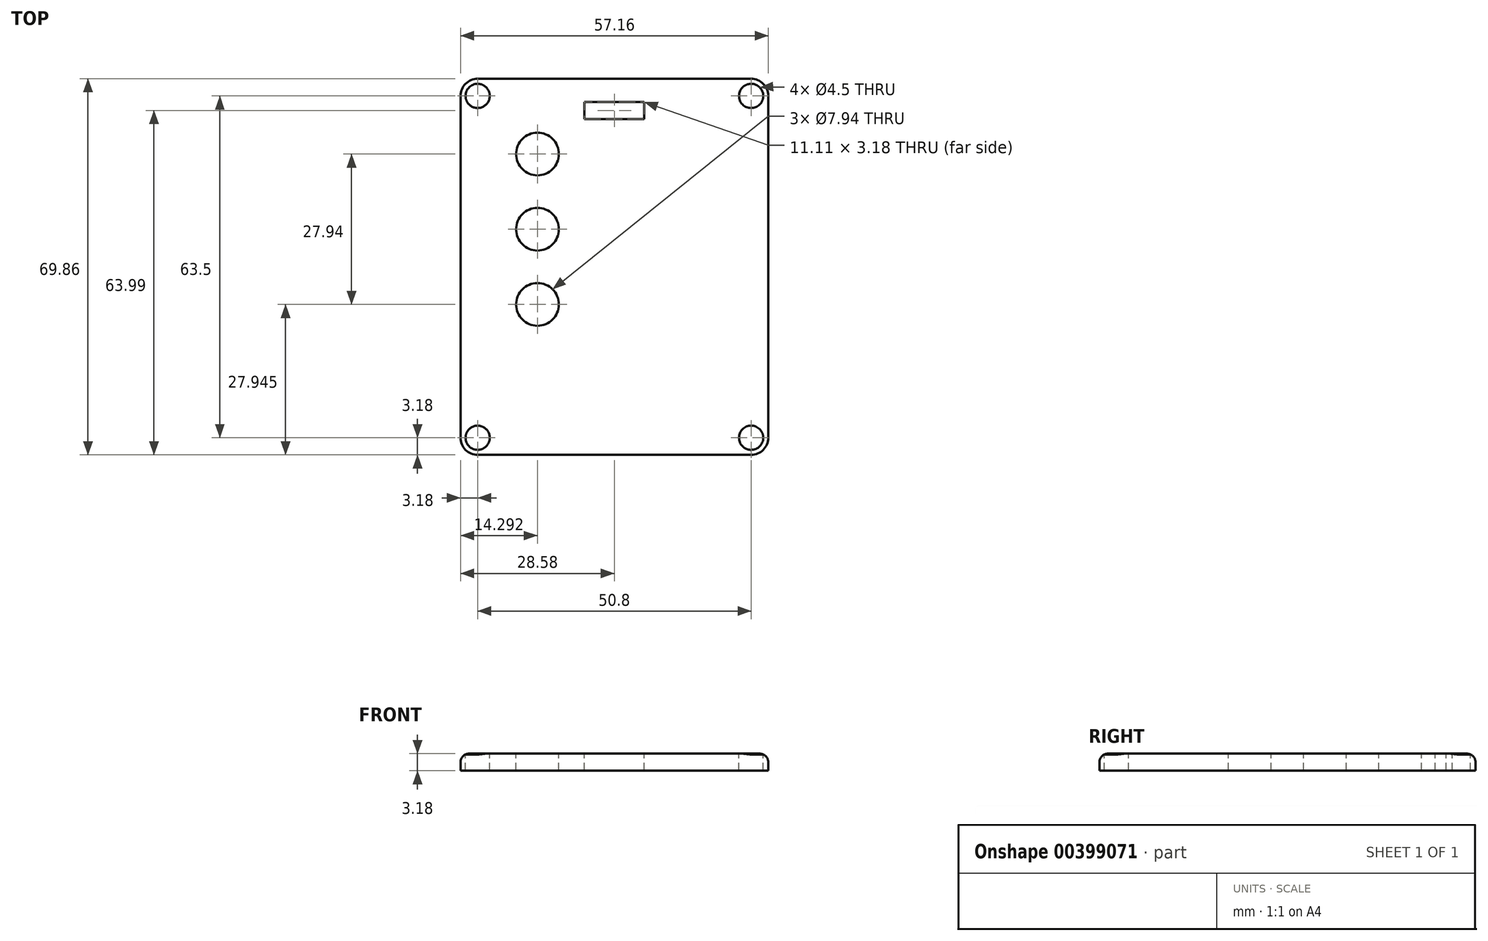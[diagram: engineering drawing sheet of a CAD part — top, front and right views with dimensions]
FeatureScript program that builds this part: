
annotation { "Feature Type Name" : "Feature", "Feature Type Description" : "" }
export const myFeature = defineFeature(function(context is Context, id is Id, definition is map)
    precondition{}
    {
        {
            var Q0;
            Q0=qCreatedBy(makeId("Top.planeOp"),FACE);
            var sketch = newSketch(context, id + "F0", { "sketchPlane" : qUnion([Q0])});
            skLineSegment(sketch, "E0.bottom", {"start": v(-25.4, 34.93) * mm, "end": v(25.4, 34.93) * mm});
            skLineSegment(sketch, "E0.top", {"start": v(-25.4, -34.93) * mm, "end": v(25.4, -34.93) * mm});
            skLineSegment(sketch, "E0.left", {"start": v(-28.58, 31.75) * mm, "end": v(-28.58, -31.75) * mm});
            skLineSegment(sketch, "E0.right", {"start": v(28.57, 31.75) * mm, "end": v(28.58, -31.75) * mm});
            skPoint(sketch, "E1.visualSharp", {"position": v(-28.58, 34.93) * mm});
            skArc(sketch, "E1.filletArc", {"start": v(-25.4, 34.93) * mm, "mid": v(-27.65, 34) * mm, "end": v(-28.58, 31.75) * mm});
            skPoint(sketch, "E2.visualSharp", {"position": v(28.57, 34.93) * mm});
            skArc(sketch, "E2.filletArc", {"start": v(28.57, 31.75) * mm, "mid": v(27.65, 34) * mm, "end": v(25.4, 34.92) * mm});
            skPoint(sketch, "E3.visualSharp", {"position": v(28.58, -34.93) * mm});
            skArc(sketch, "E3.filletArc", {"start": v(25.4, -34.93) * mm, "mid": v(27.65, -34) * mm, "end": v(28.58, -31.75) * mm});
            skPoint(sketch, "E4.visualSharp", {"position": v(-28.58, -34.93) * mm});
            skArc(sketch, "E4.filletArc", {"start": v(-28.58, -31.75) * mm, "mid": v(-27.65, -34) * mm, "end": v(-25.4, -34.93) * mm});
            skSolve(sketch);
        }
        {
            var Q0;
            Q0 = qSketchRegion(id + "F0", true);
            extrude(context, id + "F1", {"entities" : qUnion([Q0]), "depth" : 3.17 * mm});
        }
        {
            var Q0;
            Q0=makeQuery(id+"F1.opExtrude","CAP_EDGE",EDGE,{"disambiguationData":[OSD([sQuery(id+"F0.wireOp",EDGE,"E0.top")])],"isStart":false});
            var Q1;
            Q1=makeQuery(id+"F1.opExtrude","CAP_EDGE",EDGE,{"disambiguationData":[OSD([sQuery(id+"F0.wireOp",EDGE,"E0.left")])],"isStart":false});
            fillet(context, id + "F2", {"entities" : qUnion([Q0, Q1]), "radius" : 1.59 * mm, "tangentPropagation" : true, "allowEdgeOverflow" : false});
        }
        {
            var Q0;
            Q0=makeQuery(id+"F1.opExtrude","CAP_FACE",FACE,{"disambiguationData":[OSD([sQuery(id+"F0.wireOp",EDGE,"E0.bottom"),sQuery(id+"F0.wireOp",EDGE,"E0.top"),sQuery(id+"F0.wireOp",EDGE,"E0.left"),sQuery(id+"F0.wireOp",EDGE,"E0.right"),sQuery(id+"F0.wireOp",EDGE,"E1.filletArc"),sQuery(id+"F0.wireOp",EDGE,"E2.filletArc"),sQuery(id+"F0.wireOp",EDGE,"E3.filletArc"),sQuery(id+"F0.wireOp",EDGE,"E4.filletArc")])],"isStart":false});
            var sketch = newSketch(context, id + "F3", { "sketchPlane" : qUnion([Q0])});
            skCircle(sketch, "E5", {"center": v(-25.4, 31.75) * mm, "radius": 2.25 * mm});
            skCircle(sketch, "E6", {"center": v(25.4, 31.75) * mm, "radius": 2.25 * mm});
            skCircle(sketch, "E7", {"center": v(25.4, -31.75) * mm, "radius": 2.25 * mm});
            skCircle(sketch, "E8", {"center": v(-25.4, -31.75) * mm, "radius": 2.25 * mm});
            skSolve(sketch);
        }
        {
            var Q0;
            Q0 = qSketchRegion(id + "F3", true);
            extrude(context, id + "F4", {"entities" : qUnion([Q0]), "operationType" : NewBodyOperationType.REMOVE, "endBound" : BoundingType.THROUGH_ALL, "oppositeDirection" : true, "depth" : 25.4 * mm});
        }
        {
            var Q0;
            Q0=makeQuery(id+"F1.opExtrude","CAP_FACE",FACE,{"disambiguationData":[OSD([sQuery(id+"F0.wireOp",EDGE,"E0.bottom"),sQuery(id+"F0.wireOp",EDGE,"E0.top"),sQuery(id+"F0.wireOp",EDGE,"E0.left"),sQuery(id+"F0.wireOp",EDGE,"E0.right"),sQuery(id+"F0.wireOp",EDGE,"E1.filletArc"),sQuery(id+"F0.wireOp",EDGE,"E2.filletArc"),sQuery(id+"F0.wireOp",EDGE,"E3.filletArc"),sQuery(id+"F0.wireOp",EDGE,"E4.filletArc")])],"isStart":false});
            var sketch = newSketch(context, id + "F5", { "sketchPlane" : qUnion([Q0])});
            skCircle(sketch, "E9", {"center": v(-14.29, -6.98) * mm, "radius": 3.97 * mm});
            skCircle(sketch, "E10", {"center": v(-14.29, 6.98) * mm, "radius": 3.97 * mm});
            skCircle(sketch, "E11", {"center": v(-14.29, 20.96) * mm, "radius": 3.97 * mm});
            skLineSegment(sketch, "E12.bottom", {"start": v(-5.56, 30.65) * mm, "end": v(5.56, 30.65) * mm});
            skLineSegment(sketch, "E12.top", {"start": v(-5.56, 27.47) * mm, "end": v(5.56, 27.47) * mm});
            skLineSegment(sketch, "E12.left", {"start": v(-5.56, 30.65) * mm, "end": v(-5.56, 27.47) * mm});
            skLineSegment(sketch, "E12.right", {"start": v(5.56, 30.65) * mm, "end": v(5.56, 27.47) * mm});
            skSolve(sketch);
        }
        {
            var Q0;
            Q0 = qSketchRegion(id + "F5", true);
            extrude(context, id + "F6", {"entities" : qUnion([Q0]), "operationType" : NewBodyOperationType.REMOVE, "endBound" : BoundingType.THROUGH_ALL, "oppositeDirection" : true, "depth" : 25.4 * mm});
        }
    });
